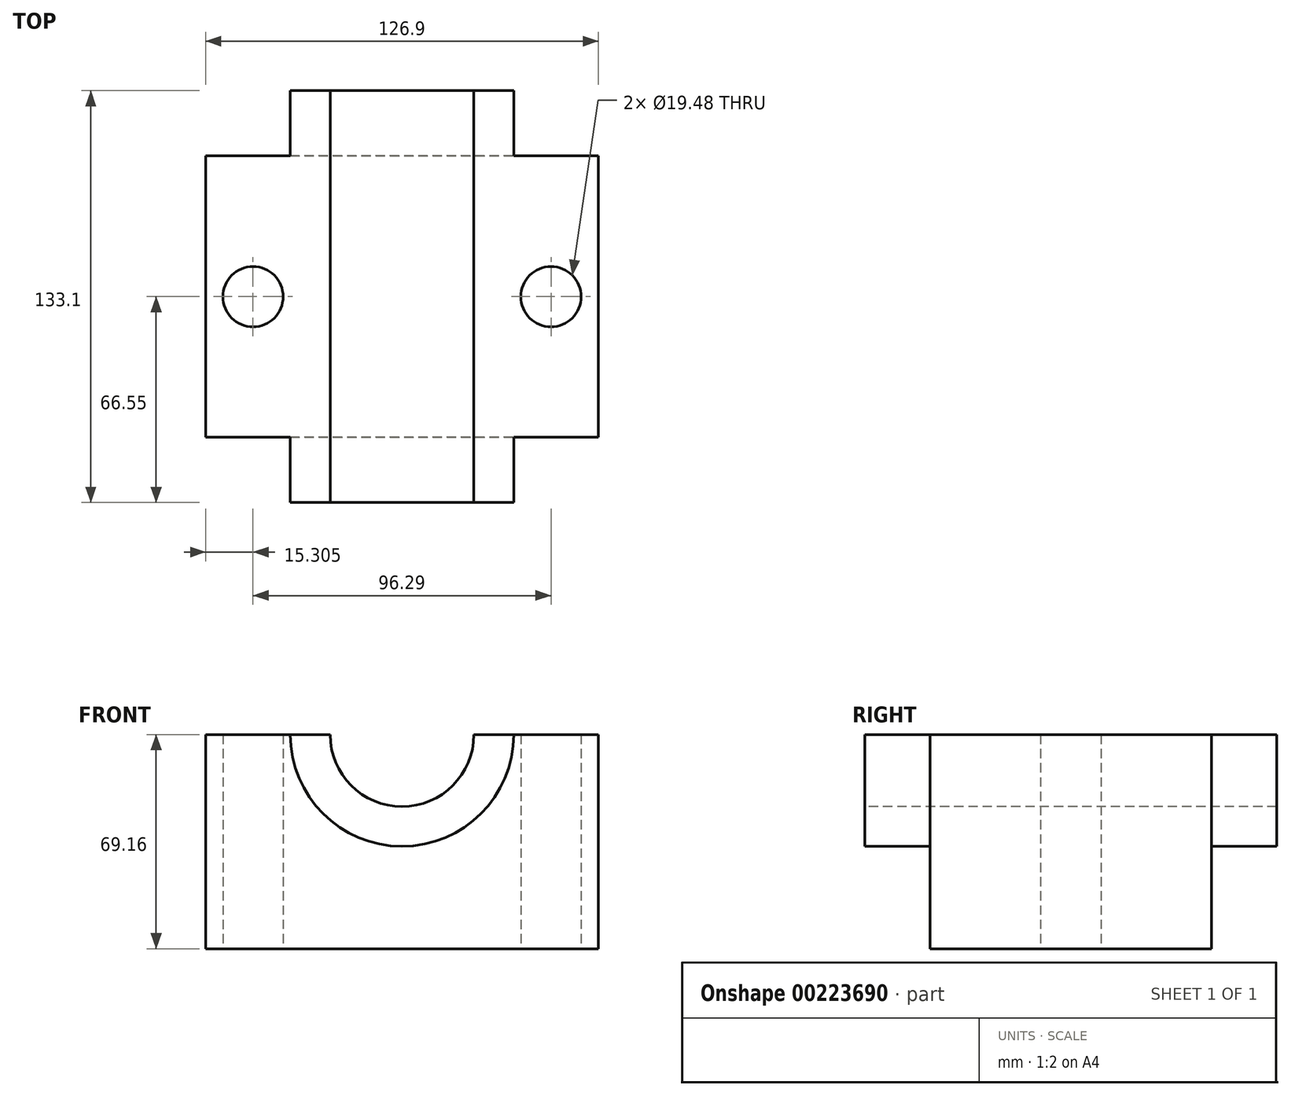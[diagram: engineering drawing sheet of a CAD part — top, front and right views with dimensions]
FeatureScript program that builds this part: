
annotation { "Feature Type Name" : "Feature", "Feature Type Description" : "" }
export const myFeature = defineFeature(function(context is Context, id is Id, definition is map)
    precondition{}
    {
        {
            var Q0;
            Q0=qCreatedBy(makeId("Front.planeOp"),FACE);
            var sketch = newSketch(context, id + "F0", { "sketchPlane" : qUnion([Q0])});
            skLineSegment(sketch, "E0.bottom", {"start": v(63.45, 69.16) * mm, "end": v(-63.45, 69.16) * mm});
            skLineSegment(sketch, "E0.top", {"start": v(63.45, -69.16) * mm, "end": v(-63.45, -69.16) * mm});
            skLineSegment(sketch, "E0.left", {"start": v(63.45, 69.16) * mm, "end": v(63.45, -69.16) * mm});
            skLineSegment(sketch, "E0.right", {"start": v(-63.45, 69.16) * mm, "end": v(-63.45, -69.16) * mm});
            skPoint(sketch, "E0.middle", {"position": v(0, 0) * mm});
            skSolve(sketch);
        }
        {
            var Q0;
            Q0 = qSketchRegion(id + "F0", true);
            extrude(context, id + "F1", {"entities" : qUnion([Q0]), "endBound" : BoundingType.SYMMETRIC, "depth" : 90.93 * mm});
        }
        {
            var Q0;
            Q0=qCreatedBy(makeId("Front.planeOp"),FACE);
            var sketch = newSketch(context, id + "F2", { "sketchPlane" : qUnion([Q0])});
            skCircle(sketch, "E1", {"center": v(0, 0) * mm, "radius": 36.09 * mm});
            skSolve(sketch);
        }
        {
            var Q0;
            Q0 = qSketchRegion(id + "F2", true);
            extrude(context, id + "F3", {"entities" : qUnion([Q0]), "operationType" : NewBodyOperationType.ADD, "endBound" : BoundingType.SYMMETRIC, "depth" : 133.1 * mm});
        }
        {
            var Q0;
            Q0=makeQuery(id+"F3.opExtrude","CAP_FACE",FACE,{"disambiguationData":[OSD([sQuery(id+"F2.wireOp",EDGE,"E1")])],"isStart":false});
            var sketch = newSketch(context, id + "F4", { "sketchPlane" : qUnion([Q0])});
            skCircle(sketch, "E2", {"center": v(0, 0) * mm, "radius": 23.2 * mm});
            skSolve(sketch);
        }
        {
            var Q0;
            Q0 = qSketchRegion(id + "F4", true);
            extrude(context, id + "F5", {"entities" : qUnion([Q0]), "operationType" : NewBodyOperationType.REMOVE, "oppositeDirection" : true, "depth" : 158 * mm});
        }
        {
            var Q0;
            Q0=qCreatedBy(makeId("Front.planeOp"),FACE);
            var sketch = newSketch(context, id + "F6", { "sketchPlane" : qUnion([Q0])});
            skLineSegment(sketch, "E3.bottom", {"start": v(-84.6, 0) * mm, "end": v(89.61, 0) * mm});
            skLineSegment(sketch, "E3.top", {"start": v(-84.6, 78.06) * mm, "end": v(89.61, 78.06) * mm});
            skLineSegment(sketch, "E3.left", {"start": v(-84.6, 0) * mm, "end": v(-84.6, 78.06) * mm});
            skLineSegment(sketch, "E3.right", {"start": v(89.61, 0) * mm, "end": v(89.61, 78.06) * mm});
            skSolve(sketch);
        }
        {
            var Q0;
            Q0 = qSketchRegion(id + "F6", true);
            extrude(context, id + "F7", {"entities" : qUnion([Q0]), "operationType" : NewBodyOperationType.REMOVE, "endBound" : BoundingType.SYMMETRIC, "oppositeDirection" : true, "depth" : 151.9 * mm});
        }
        {
            var Q0;
            Q0=makeQuery(id+"F1.opExtrude","SWEPT_FACE",FACE,{"disambiguationData":[OSD([sQuery(id+"F0.wireOp",EDGE,"E0.top")])]});
            var sketch = newSketch(context, id + "F8", { "sketchPlane" : qUnion([Q0])});
            skCircle(sketch, "E4", {"center": v(48.15, 0) * mm, "radius": 9.74 * mm});
            skCircle(sketch, "E5.MirrorC", {"center": v(-48.15, 0) * mm, "radius": 9.74 * mm});
            skSolve(sketch);
        }
        {
            var Q0;
            Q0 = qSketchRegion(id + "F8", true);
            extrude(context, id + "F9", {"entities" : qUnion([Q0]), "operationType" : NewBodyOperationType.REMOVE, "oppositeDirection" : true, "depth" : 80.26 * mm});
        }
    });
